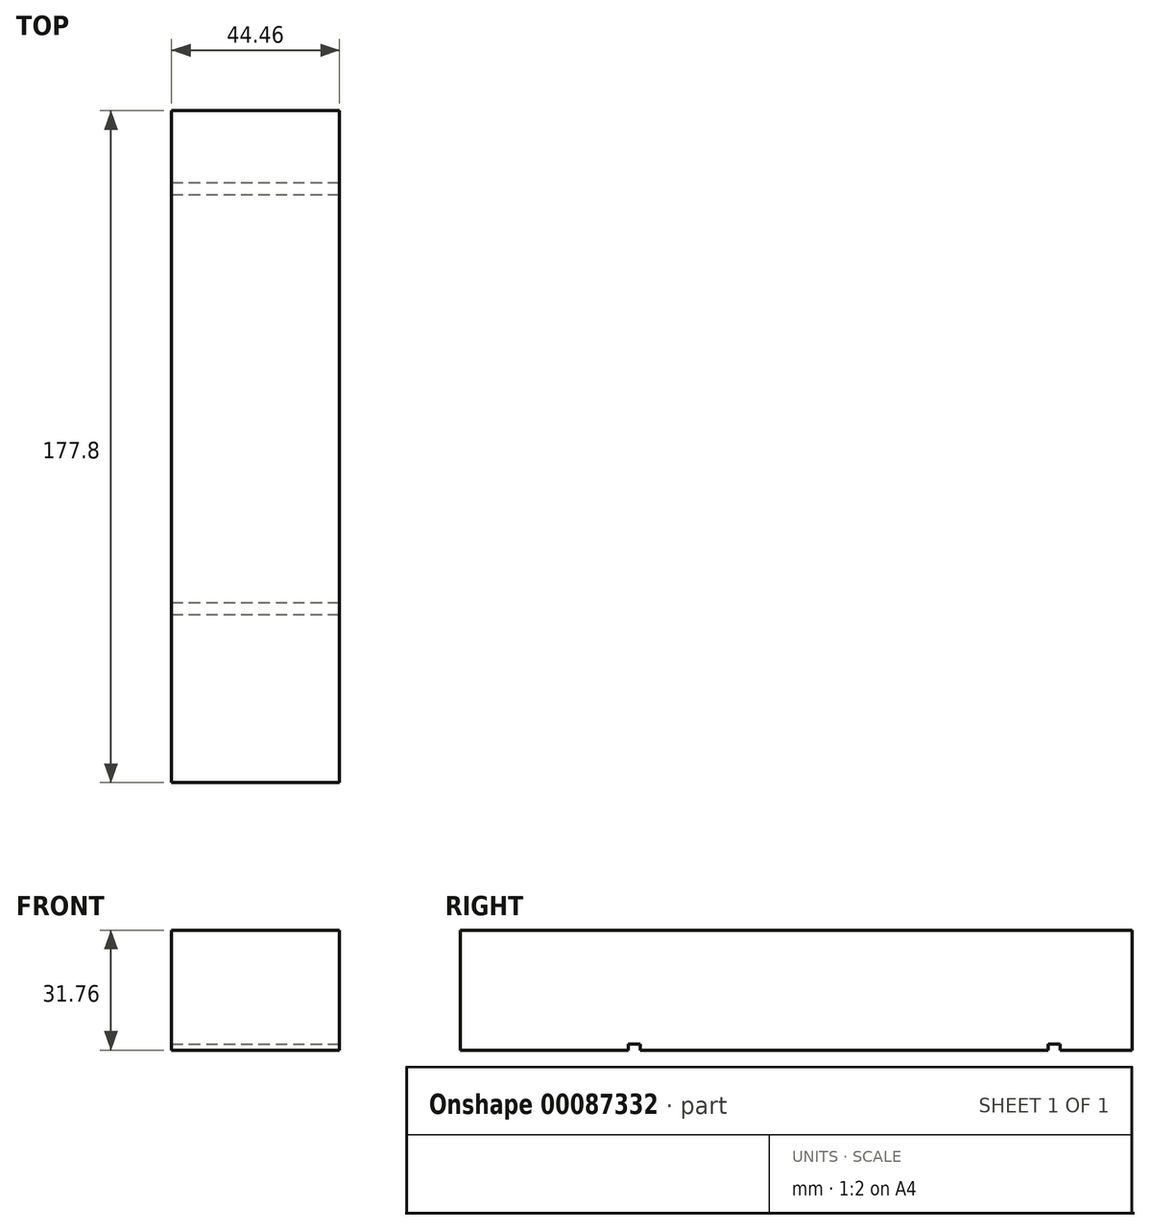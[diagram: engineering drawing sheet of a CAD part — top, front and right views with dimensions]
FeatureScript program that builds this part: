
annotation { "Feature Type Name" : "Feature", "Feature Type Description" : "" }
export const myFeature = defineFeature(function(context is Context, id is Id, definition is map)
    precondition{}
    {
        {
            var Q0;
            Q0=qCreatedBy(makeId("Front.planeOp"),FACE);
            var sketch = newSketch(context, id + "F0", { "sketchPlane" : qUnion([Q0])});
            skLineSegment(sketch, "E0.bottom", {"start": v(22.22, 15.88) * mm, "end": v(-22.23, 15.88) * mm});
            skLineSegment(sketch, "E0.top", {"start": v(22.23, -15.88) * mm, "end": v(-22.22, -15.88) * mm});
            skLineSegment(sketch, "E0.left", {"start": v(22.22, 15.88) * mm, "end": v(22.23, -15.88) * mm});
            skLineSegment(sketch, "E0.right", {"start": v(-22.23, 15.88) * mm, "end": v(-22.22, -15.88) * mm});
            skPoint(sketch, "E0.middle", {"position": v(0, 0) * mm});
            skSolve(sketch);
        }
        {
            var Q0;
            Q0=makeQuery(id+"F0.imprint","IMPRINT",FACE,{"disambiguationData":[TD([[makeQuery(id+"F0.imprint","IMPRINT",EDGE,{"derivedFrom":sQuery(id+"F0.wireOp",EDGE,"E0.bottom")}),1.0]])]});
            extrude(context, id + "F1", {"entities" : qUnion([Q0]), "oppositeDirection" : true, "depth" : 177.8 * mm});
        }
        {
            var Q0;
            Q0=makeQuery(id+"F1.opExtrude","SWEPT_FACE",FACE,{"disambiguationData":[OSD([sQuery(id+"F0.wireOp",EDGE,"E0.left")])]});
            var sketch = newSketch(context, id + "F2", { "sketchPlane" : qUnion([Q0])});
            skLineSegment(sketch, "E1.bottom", {"start": v(44.45, -15.88) * mm, "end": v(47.62, -15.88) * mm});
            skLineSegment(sketch, "E2.bottom", {"start": v(155.57, -15.88) * mm, "end": v(158.75, -15.88) * mm});
            skArc(sketch, "E3", {"start": v(47.62, -15.88) * mm, "mid": v(46.04, -14.29) * mm, "end": v(44.45, -15.88) * mm});
            skArc(sketch, "E4", {"start": v(158.75, -15.88) * mm, "mid": v(157.16, -14.29) * mm, "end": v(155.57, -15.88) * mm});
            skPoint(sketch, "E5.oppositeSnap0", {"position": v(46.04, -14.29) * mm});
            skLineSegment(sketch, "E5.top", {"start": v(44.45, -14.29) * mm, "end": v(47.62, -14.29) * mm});
            skLineSegment(sketch, "E5.left", {"start": v(44.45, -15.88) * mm, "end": v(44.45, -14.29) * mm});
            skLineSegment(sketch, "E5.right", {"start": v(47.62, -15.88) * mm, "end": v(47.62, -14.29) * mm});
            skLineSegment(sketch, "E6.top", {"start": v(155.58, -14.29) * mm, "end": v(158.75, -14.29) * mm});
            skLineSegment(sketch, "E6.left", {"start": v(155.57, -15.88) * mm, "end": v(155.57, -14.29) * mm});
            skLineSegment(sketch, "E6.right", {"start": v(158.75, -15.88) * mm, "end": v(158.75, -14.29) * mm});
            skSolve(sketch);
        }
        {
            var Q0;
            {var subQ0=sQuery(id+"F2.wireOp",EDGE,"E1.bottom");Q0=makeQuery(id+"F2.imprint","IMPRINT",FACE,{"disambiguationData":[TD([[makeQuery(id+"F2.imprint","IMPRINT",EDGE,{"derivedFrom":subQ0}),-1.0]])]});}
            var Q1;
            {var subQ0=sQuery(id+"F2.wireOp",EDGE,"E5.right");Q1=makeQuery(id+"F2.imprint","IMPRINT",FACE,{"disambiguationData":[TD([[makeQuery(id+"F2.imprint","IMPRINT",EDGE,{"derivedFrom":subQ0}),1.0]])]});}
            var Q2;
            {var subQ0=sQuery(id+"F2.wireOp",EDGE,"E5.left");Q2=makeQuery(id+"F2.imprint","IMPRINT",FACE,{"disambiguationData":[TD([[makeQuery(id+"F2.imprint","IMPRINT",EDGE,{"derivedFrom":subQ0}),-1.0]])]});}
            var Q3;
            {var subQ0=sQuery(id+"F2.wireOp",EDGE,"E2.bottom");Q3=makeQuery(id+"F2.imprint","IMPRINT",FACE,{"disambiguationData":[TD([[makeQuery(id+"F2.imprint","IMPRINT",EDGE,{"derivedFrom":subQ0}),-1.0]])]});}
            var Q4;
            {var subQ0=sQuery(id+"F2.wireOp",EDGE,"E6.right");Q4=makeQuery(id+"F2.imprint","IMPRINT",FACE,{"disambiguationData":[TD([[makeQuery(id+"F2.imprint","IMPRINT",EDGE,{"derivedFrom":subQ0}),1.0]])]});}
            var Q5;
            {var subQ0=sQuery(id+"F2.wireOp",EDGE,"E6.left");Q5=makeQuery(id+"F2.imprint","IMPRINT",FACE,{"disambiguationData":[TD([[makeQuery(id+"F2.imprint","IMPRINT",EDGE,{"derivedFrom":subQ0}),-1.0]])]});}
            extrude(context, id + "F3", {"entities" : qUnion([Q0, Q1, Q2, Q3, Q4, Q5]), "operationType" : NewBodyOperationType.REMOVE, "endBound" : BoundingType.THROUGH_ALL, "oppositeDirection" : true, "depth" : 25.4 * mm});
        }
    });
